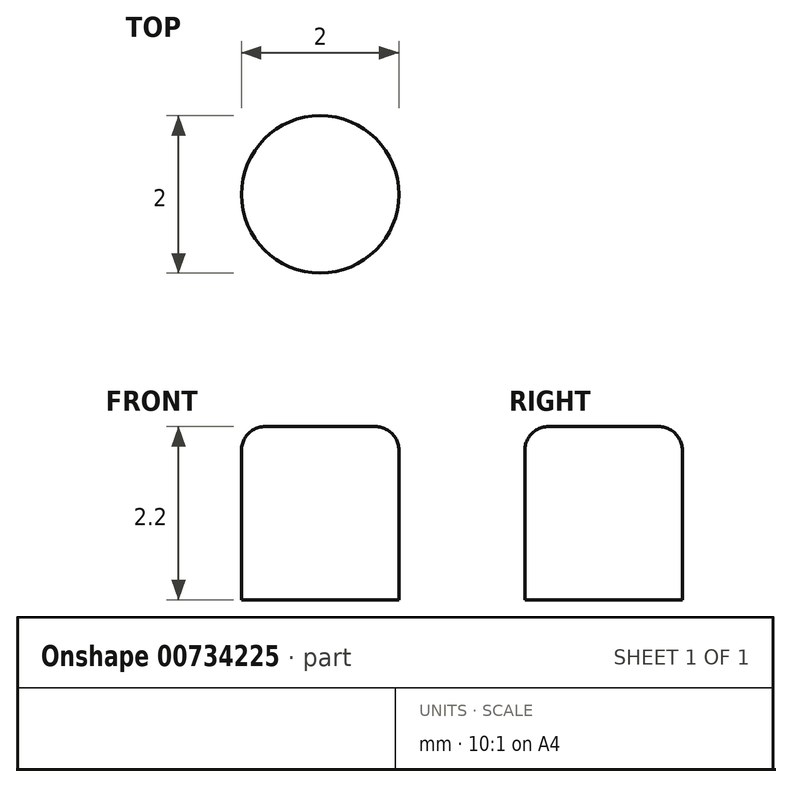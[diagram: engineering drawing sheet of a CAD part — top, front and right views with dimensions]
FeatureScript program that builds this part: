
annotation { "Feature Type Name" : "Feature", "Feature Type Description" : "" }
export const myFeature = defineFeature(function(context is Context, id is Id, definition is map)
    precondition{}
    {
        {
            var Q0;
            Q0=qCreatedBy(makeId("Top.planeOp"),FACE);
            var sketch = newSketch(context, id + "F0", { "sketchPlane" : qUnion([Q0])});
            skCircle(sketch, "E0", {"center": v(0, 0) * mm, "radius": 1 * mm});
            skSolve(sketch);
        }
        {
            var Q0;
            Q0=qSketchRegion(id+"F0",true);
            extrude(context, id + "F1", {"entities" : qUnion([Q0]), "depth" : 2.2 * mm, "offsetDistance" : 25 * mm});
        }
        {
            var Q0;
            Q0=makeQuery(id+"F1.opExtrude","CAP_EDGE",EDGE,{"disambiguationData":[OSD([sQuery(id+"F0.wireOp",EDGE,"E0")])],"isStart":false});
            fillet(context, id + "F2", {"entities" : qUnion([Q0]), "radius" : 0.3 * mm, "tangentPropagation" : true, "allowEdgeOverflow" : false});
        }
    });
